# Revit family: Electronics_Visual-TVs_ViewSonic_The-ViewSonicR-CDX4952-Commercial-Displa
name_source: partatom
category: Electrical Equipment
revit_build: Autodesk Revit 2015 (Build: 20140606_1530(x64)
units: mm (PartAtom-declared; Revit-internal decimal feet)

## types (1)
- CDX4952
    Assembly Code = D50
    BIMobject category = Visual - TVs
    BIMobject category code = electronics-visual-tvs
    BIMobject main category = Electronics
    BIMobject main category code = electronics
    BOSUseNativeGeometries = 1
    Brand url = https://www.viewsonic.com
    Covering Color = Plastic - Viewsonic - Black
    Description = With stunning brightness, vibrant images, and multi-screen tiling, the ViewSonic® CDX4952 49" (48.5" viewable) commercial display is your ideal tool for creating video walls that wow! With up to 10x10 tiling installation, and an ultra-narrow bezel that measures only 3.5mm between combined displays, the CDX4952 delivers nearly seamless, high-impact messaging that helps you to astonish, inspire, and inform. Featuring full metal construction and a scratch-resistant tempered glass screen, this durable commercial-grade display delivers reliable messaging 24 hours a day, 7 days a week. With Full HD 1080p resolution, 450-nit brightness, SuperClear® technology for wide viewing angles, and dual 10W stereo speakers, the CDX492 delivers sharp, vivid images with incredible sound for superior multimedia performance.
    Design country = Taiwan
    Edition number = 1
    Keynote = V90
    Manufacturer = ViewSonic
    Manufacturer country = Taiwan
    Manufacturer name = ViewSonic
    Model = viewsonic_cdx4952
    Product Guid = 4e3570ff-0cce-42ca-a652-de7d579f80d1
    Product SKU = viewsonic_cdx4952
    Product data url = https://bimobject.com
    Product family = Electronics
    Product group = Commercial Displays
    Product name = The ViewSonic® CDX4952 Commercial Display
    Product url = https://www.viewsonic.com
    QR code = http://bimobject.com
    URL = www.viewsonic.com

## geometry (parser evidence)
native form markers: Sweep x3
no freeform markers — native parametric forms only
